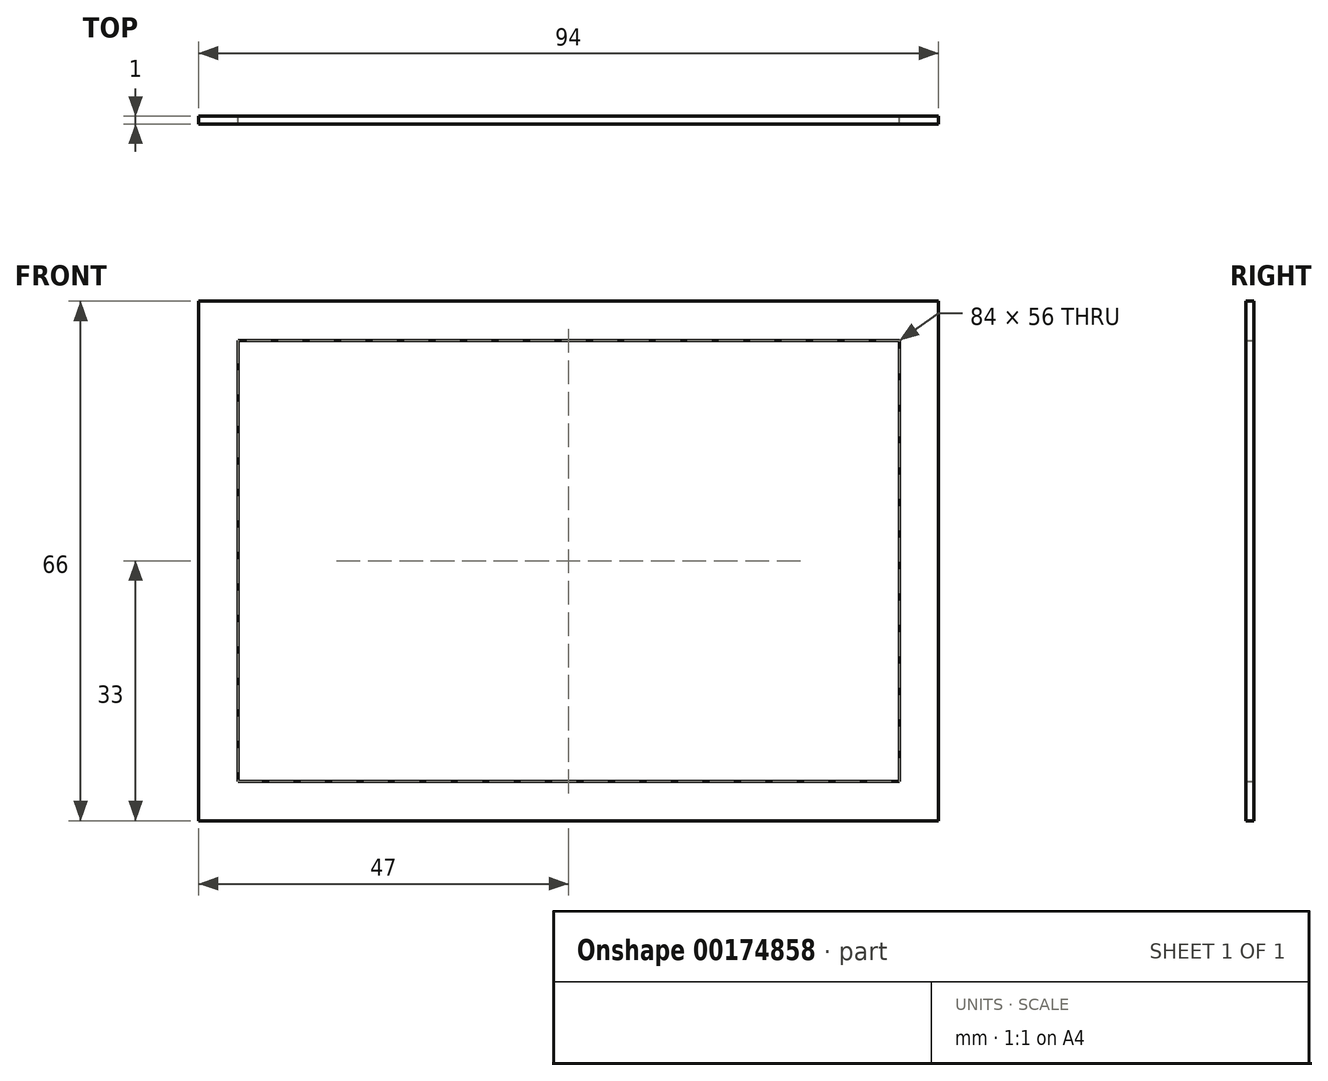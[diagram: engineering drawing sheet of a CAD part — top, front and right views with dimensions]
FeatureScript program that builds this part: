
annotation { "Feature Type Name" : "Feature", "Feature Type Description" : "" }
export const myFeature = defineFeature(function(context is Context, id is Id, definition is map)
    precondition{}
    {
        {
            var Q0;
            Q0=qCreatedBy(makeId("Front.planeOp"),FACE);
            var sketch = newSketch(context, id + "F0", { "sketchPlane" : qUnion([Q0])});
            skLineSegment(sketch, "E0.bottom", {"start": v(47, 33) * mm, "end": v(-47, 33) * mm});
            skLineSegment(sketch, "E0.top", {"start": v(47, -33) * mm, "end": v(-47, -33) * mm});
            skLineSegment(sketch, "E0.left", {"start": v(47, 33) * mm, "end": v(47, -33) * mm});
            skLineSegment(sketch, "E0.right", {"start": v(-47, 33) * mm, "end": v(-47, -33) * mm});
            skPoint(sketch, "E0.middle", {"position": v(0, 0) * mm});
            skLineSegment(sketch, "E1.bottom", {"start": v(42, 28) * mm, "end": v(-42, 28) * mm});
            skLineSegment(sketch, "E1.top", {"start": v(42, -28) * mm, "end": v(-42, -28) * mm});
            skLineSegment(sketch, "E1.left", {"start": v(42, 28) * mm, "end": v(42, -28) * mm});
            skLineSegment(sketch, "E1.right", {"start": v(-42, 28) * mm, "end": v(-42, -28) * mm});
            skSolve(sketch);
        }
        {
            var Q0;
            Q0 = qSketchRegion(id + "F0", true);
            extrude(context, id + "F1", {"entities" : qUnion([Q0]), "depth" : 1 * mm});
        }
    });
